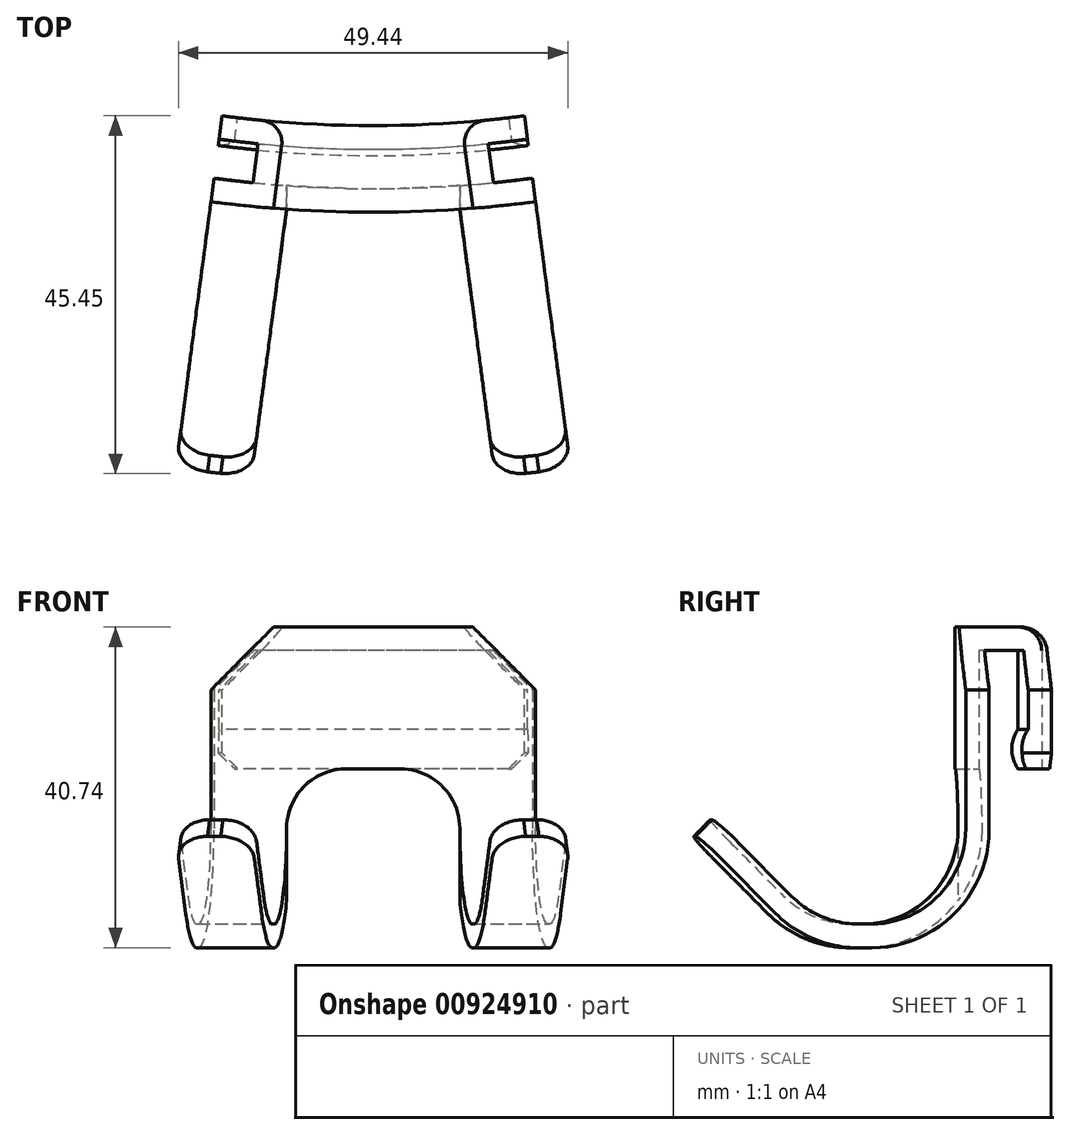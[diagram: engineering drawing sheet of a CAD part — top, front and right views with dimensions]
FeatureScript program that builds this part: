
annotation { "Feature Type Name" : "Feature", "Feature Type Description" : "" }
export const myFeature = defineFeature(function(context is Context, id is Id, definition is map)
    precondition{}
    {
        {
            var Q0;
            Q0=qCreatedBy(makeId("Right.planeOp"),FACE);
            var sketch = newSketch(context, id + "F0", { "sketchPlane" : qUnion([Q0])});
            skLineSegment(sketch, "E0", {"start": v(0, 0) * mm, "end": v(3, 0) * mm});
            skLineSegment(sketch, "E1", {"start": v(3, 0) * mm, "end": v(3, 13) * mm});
            skLineSegment(sketch, "E2", {"start": v(3, 13) * mm, "end": v(-8, 13) * mm});
            skLineSegment(sketch, "E3", {"start": v(-8, 13) * mm, "end": v(-8, -27.74) * mm});
            skLineSegment(sketch, "E4", {"start": v(0, 0) * mm, "end": v(0, 10) * mm});
            skLineSegment(sketch, "E5", {"start": v(0, 10) * mm, "end": v(-5, 10) * mm});
            skLineSegment(sketch, "E6", {"start": v(-5, 10) * mm, "end": v(-5, -27.74) * mm});
            skLineSegment(sketch, "E7", {"start": v(-5, -27.74) * mm, "end": v(-8, -27.74) * mm});
            skLineSegment(sketch, "E8", {"start": v(-8, -27.74) * mm, "end": v(-28, -27.74) * mm});
            skLineSegment(sketch, "E9", {"start": v(-28, -27.74) * mm, "end": v(-42.14, -13.6) * mm});
            skLineSegment(sketch, "E10", {"start": v(-42.14, -13.6) * mm, "end": v(-40.02, -11.48) * mm});
            skLineSegment(sketch, "E11", {"start": v(-40.02, -11.48) * mm, "end": v(-26.76, -24.74) * mm});
            skLineSegment(sketch, "E12", {"start": v(-26.76, -24.74) * mm, "end": v(-8, -24.74) * mm});
            skLineSegment(sketch, "E13", {"start": v(-5, 10) * mm, "end": v(-5, 13) * mm});
            skLineSegment(sketch, "E14", {"start": v(150, 0) * mm, "end": v(150, 35.9) * mm, "construction": true});
            skLineSegment(sketch, "E15", {"start": v(3, 0) * mm, "end": v(3, -5) * mm});
            skLineSegment(sketch, "E16", {"start": v(3, -5) * mm, "end": v(0, -5) * mm});
            skLineSegment(sketch, "E17", {"start": v(0, -5) * mm, "end": v(0, 0) * mm});
            skArc(sketch, "E18", {"start": v(0, 0) * mm, "mid": v(-0.8, -2.5) * mm, "end": v(0, -5) * mm});
            skSolve(sketch);
        }
        {
            var Q0;
            Q0=makeQuery(id+"F0.imprint","IMPRINT",FACE,{"disambiguationData":[TD([[makeQuery(id+"F0.imprint","IMPRINT",EDGE,{"derivedFrom":sQuery(id+"F0.wireOp",EDGE,"E0")}),1.0]])]});
            var Q1;
            Q1=makeQuery(id+"F0.imprint","IMPRINT",FACE,{"disambiguationData":[TD([[makeQuery(id+"F0.imprint","IMPRINT",EDGE,{"derivedFrom":sQuery(id+"F0.wireOp",EDGE,"E17")}),1.0]])]});
            var Q2;
            Q2=makeQuery(id+"F0.imprint","IMPRINT",FACE,{"disambiguationData":[TD([[makeQuery(id+"F0.imprint","IMPRINT",EDGE,{"derivedFrom":sQuery(id+"F0.wireOp",EDGE,"E0")}),-1.0]])]});
            var Q3;
            Q3=sQuery(id+"F0.wireOp",EDGE,"E14");
            revolve(context, id + "F1", {"surfaceOperationType" : NewSurfaceOperationType.NEW, "entities" : qUnion([Q0, Q1, Q2]), "axis" : qUnion([Q3]), "revolveType" : RevolveType.SYMMETRIC, "angle" : 15 * degree});
        }
        {
            var Q0;
            Q0=makeQuery(id+"F0.imprint","IMPRINT",FACE,{"disambiguationData":[TD([[makeQuery(id+"F0.imprint","IMPRINT",EDGE,{"derivedFrom":sQuery(id+"F0.wireOp",EDGE,"E6")}),-1.0]])]});
            var Q1;
            {var subQ0=sQuery(id+"F0.wireOp",EDGE,"E8");Q1=makeQuery(id+"F0.imprint","IMPRINT",FACE,{"disambiguationData":[TD([[makeQuery(id+"F0.imprint","IMPRINT",EDGE,{"derivedFrom":subQ0}),-1.0]])]});}
            var Q2;
            Q2=sQuery(id+"F0.wireOp",EDGE,"E14");
            revolve(context, id + "F2", {"operationType" : NewBodyOperationType.ADD, "surfaceOperationType" : NewSurfaceOperationType.NEW, "entities" : qUnion([Q0, Q1]), "axis" : qUnion([Q2]), "revolveType" : RevolveType.SYMMETRIC, "angle" : 15 * degree});
        }
        {
            var Q0;
            Q0=makeQuery(id+"F2.opRevolve","SWEPT_FACE",FACE,{"disambiguationData":[OSD([sQuery(id+"F0.wireOp",EDGE,"E12")])]});
            var sketch = newSketch(context, id + "F3", { "sketchPlane" : qUnion([Q0])});
            skLineSegment(sketch, "E19", {"start": v(-11, -7.62) * mm, "end": v(-15.57, -42.32) * mm});
            skLineSegment(sketch, "E20", {"start": v(-15.57, -42.32) * mm, "end": v(15.57, -42.32) * mm});
            skLineSegment(sketch, "E21", {"start": v(15.57, -42.32) * mm, "end": v(11, -7.62) * mm});
            skPoint(sketch, "E22", {"position": v(0, -42.32) * mm});
            skSolve(sketch);
        }
        {
            var Q0;
            Q0 = qSketchRegion(id + "F3", true);
            var Q1;
            {var subQ0=sQuery(id+"F3.wireOp",EDGE,"E19");var subQ1=sQuery(id+"F0.wireOp",EDGE,"E12");var subQ2=makeQuery(id+"F2.opRevolve","SWEPT_EDGE",EDGE,{"disambiguationData":[OSD([sQuery(id+"F0.wireOp",EDGE,"E3"),subQ1])]});var subQ3=makeQuery(id+"F3.imprint","INTERSECT",VERTEX,{"derivedFrom":[subQ2,subQ0]});Q1=makeQuery(id+"F3.imprint","IMPRINT",FACE,{"disambiguationData":[TD([[makeQuery(id+"F3.imprint","IMPRINT",EDGE,{"disambiguationData":[TD([[subQ3,-1.0]])],"derivedFrom":subQ0}),1.0]])]});}
            var Q2;
            {var subQ0=sQuery(id+"F3.wireOp",EDGE,"E20");Q2=makeQuery(id+"F3.imprint","IMPRINT",FACE,{"disambiguationData":[TD([[makeQuery(id+"F3.imprint","IMPRINT",EDGE,{"derivedFrom":subQ0}),1.0]])]});}
            extrude(context, id + "F4", {"entities" : qUnion([Q0, Q1, Q2]), "operationType" : NewBodyOperationType.REMOVE, "depth" : 81.8 * mm, "offsetDistance" : 25 * mm, "symmetric" : true});
        }
        {
            var Q0;
            {var subQ0=sQuery(id+"F0.wireOp",EDGE,"E12");var subQ1=sQuery(id+"F0.wireOp",EDGE,"E3");Q0=makeQuery(id+"F4.boolean.opBoolean","SPLIT",EDGE,{"disambiguationData":[TD([makeQuery(id+"F4.opExtrude","SWEPT_FACE",FACE,{"disambiguationData":[OSD([sQuery(id+"F3.wireOp",EDGE,"E19")])]})])],"derivedFrom":makeQuery(id+"F2.opRevolve","SWEPT_EDGE",EDGE,{"disambiguationData":[OSD([subQ1,subQ0])]})});}
            var Q1;
            {var subQ0=sQuery(id+"F0.wireOp",EDGE,"E12");var subQ1=sQuery(id+"F0.wireOp",EDGE,"E3");Q1=makeQuery(id+"F4.boolean.opBoolean","SPLIT",EDGE,{"disambiguationData":[TD([makeQuery(id+"F4.opExtrude","SWEPT_FACE",FACE,{"disambiguationData":[OSD([sQuery(id+"F3.wireOp",EDGE,"E21")])]})])],"derivedFrom":makeQuery(id+"F2.opRevolve","SWEPT_EDGE",EDGE,{"disambiguationData":[OSD([subQ1,subQ0])]})});}
            var Q2;
            {var subQ0=sQuery(id+"F0.wireOp",EDGE,"E12");var subQ1=sQuery(id+"F0.wireOp",EDGE,"E11");Q2=makeQuery(id+"F4.boolean.opBoolean","SPLIT",EDGE,{"disambiguationData":[TD([makeQuery(id+"F4.opExtrude","SWEPT_FACE",FACE,{"disambiguationData":[OSD([sQuery(id+"F3.wireOp",EDGE,"E19")])]})])],"derivedFrom":makeQuery(id+"F2.opRevolve","SWEPT_EDGE",EDGE,{"disambiguationData":[OSD([subQ1,subQ0])]})});}
            var Q3;
            {var subQ0=sQuery(id+"F0.wireOp",EDGE,"E12");var subQ1=sQuery(id+"F0.wireOp",EDGE,"E11");Q3=makeQuery(id+"F4.boolean.opBoolean","SPLIT",EDGE,{"disambiguationData":[TD([makeQuery(id+"F4.opExtrude","SWEPT_FACE",FACE,{"disambiguationData":[OSD([sQuery(id+"F3.wireOp",EDGE,"E21")])]})])],"derivedFrom":makeQuery(id+"F2.opRevolve","SWEPT_EDGE",EDGE,{"disambiguationData":[OSD([subQ1,subQ0])]})});}
            fillet(context, id + "F5", {"entities" : qUnion([Q0, Q1, Q2, Q3]), "radius" : 12.14 * mm, "tangentPropagation" : true, "allowEdgeOverflow" : false});
        }
        {
            var Q0;
            Q0=makeQuery(id+"F2.opRevolve","SWEPT_EDGE",EDGE,{"disambiguationData":[OSD([sQuery(id+"F0.wireOp",EDGE,"E6"),sQuery(id+"F0.wireOp",EDGE,"E7")])]});
            var Q1;
            {var subQ0=sQuery(id+"F0.wireOp",EDGE,"E9");var subQ1=sQuery(id+"F0.wireOp",EDGE,"E8");Q1=makeQuery(id+"F4.boolean.opBoolean","SPLIT",EDGE,{"disambiguationData":[TD([makeQuery(id+"F4.opExtrude","SWEPT_FACE",FACE,{"disambiguationData":[OSD([sQuery(id+"F3.wireOp",EDGE,"E21")])]})])],"derivedFrom":makeQuery(id+"F2.opRevolve","SWEPT_EDGE",EDGE,{"disambiguationData":[OSD([subQ1,subQ0])]})});}
            var Q2;
            {var subQ0=sQuery(id+"F0.wireOp",EDGE,"E9");var subQ1=sQuery(id+"F0.wireOp",EDGE,"E8");Q2=makeQuery(id+"F4.boolean.opBoolean","SPLIT",EDGE,{"disambiguationData":[TD([makeQuery(id+"F4.opExtrude","SWEPT_FACE",FACE,{"disambiguationData":[OSD([sQuery(id+"F3.wireOp",EDGE,"E19")])]})])],"derivedFrom":makeQuery(id+"F2.opRevolve","SWEPT_EDGE",EDGE,{"disambiguationData":[OSD([subQ1,subQ0])]})});}
            fillet(context, id + "F6", {"entities" : qUnion([Q0, Q1, Q2]), "radius" : 15 * mm, "tangentPropagation" : true, "allowEdgeOverflow" : false});
        }
        {
            var Q0;
            Q0=makeQuery(id+"F2.opRevolve","CAP_EDGE",EDGE,{"disambiguationData":[OSD([sQuery(id+"F0.wireOp",EDGE,"E10")])],"isStart":true});
            var Q1;
            Q1=makeQuery(id+"F4.boolean.opBoolean","INTERSECT",EDGE,{"derivedFrom":[makeQuery(id+"F2.opRevolve","SWEPT_FACE",FACE,{"disambiguationData":[OSD([sQuery(id+"F0.wireOp",EDGE,"E10")])]}),makeQuery(id+"F4.opExtrude","SWEPT_FACE",FACE,{"disambiguationData":[OSD([sQuery(id+"F3.wireOp",EDGE,"E19")])]})]});
            var Q2;
            Q2=makeQuery(id+"F4.boolean.opBoolean","INTERSECT",EDGE,{"derivedFrom":[makeQuery(id+"F2.opRevolve","SWEPT_FACE",FACE,{"disambiguationData":[OSD([sQuery(id+"F0.wireOp",EDGE,"E10")])]}),makeQuery(id+"F4.opExtrude","SWEPT_FACE",FACE,{"disambiguationData":[OSD([sQuery(id+"F3.wireOp",EDGE,"E21")])]})]});
            var Q3;
            Q3=makeQuery(id+"F2.opRevolve","CAP_EDGE",EDGE,{"disambiguationData":[OSD([sQuery(id+"F0.wireOp",EDGE,"E10")])],"isStart":false});
            fillet(context, id + "F7", {"entities" : qUnion([Q0, Q1, Q2, Q3]), "radius" : 4 * mm, "tangentPropagation" : true, "allowEdgeOverflow" : false});
        }
        {
            var Q0;
            Q0=qCreatedBy(makeId("Front.planeOp"),FACE);
            var sketch = newSketch(context, id + "F8", { "sketchPlane" : qUnion([Q0])});
            skPoint(sketch, "E23.0", {"position": v(-11, -12.6) * mm});
            skPoint(sketch, "E24.0", {"position": v(11, -12.6) * mm});
            skPoint(sketch, "E25.0", {"position": v(11, -21.74) * mm});
            skPoint(sketch, "E26.0", {"position": v(-11, -21.74) * mm});
            skLineSegment(sketch, "E27.bottom", {"start": v(-11, -5) * mm, "end": v(11, -5) * mm});
            skLineSegment(sketch, "E27.top", {"start": v(-11, -21.74) * mm, "end": v(11, -21.74) * mm});
            skLineSegment(sketch, "E27.left", {"start": v(-11, -5) * mm, "end": v(-11, -21.74) * mm});
            skLineSegment(sketch, "E27.right", {"start": v(11, -5) * mm, "end": v(11, -21.74) * mm});
            skLineSegment(sketch, "E28.0", {"start": v(19.19, -5) * mm, "end": v(-19.19, -5) * mm});
            skSolve(sketch);
        }
        {
            var Q0;
            Q0 = qSketchRegion(id + "F8", true);
            extrude(context, id + "F9", {"entities" : qUnion([Q0]), "operationType" : NewBodyOperationType.REMOVE, "endBound" : BoundingType.THROUGH_ALL, "depth" : 25 * mm, "offsetDistance" : 25 * mm});
        }
        {
            var Q0;
            Q0=makeQuery(id+"F9.boolean.opBoolean","COPY",EDGE,{"derivedFrom":makeQuery(id+"F9.opExtrude","SWEPT_EDGE",EDGE,{"disambiguationData":[OSD([sQuery(id+"F8.wireOp",EDGE,"E27.bottom"),sQuery(id+"F8.wireOp",EDGE,"E27.left")])]})});
            var Q1;
            Q1=makeQuery(id+"F9.boolean.opBoolean","COPY",EDGE,{"derivedFrom":makeQuery(id+"F9.opExtrude","SWEPT_EDGE",EDGE,{"disambiguationData":[OSD([sQuery(id+"F8.wireOp",EDGE,"E27.bottom"),sQuery(id+"F8.wireOp",EDGE,"E27.right")])]})});
            fillet(context, id + "F10", {"entities" : qUnion([Q0, Q1]), "radius" : 7.6 * mm, "tangentPropagation" : true, "allowEdgeOverflow" : false});
        }
        {
            var Q0;
            Q0=makeQuery(id+"F1.opRevolve","SWEPT_EDGE",EDGE,{"disambiguationData":[OSD([sQuery(id+"F0.wireOp",EDGE,"E1"),sQuery(id+"F0.wireOp",EDGE,"E2")])]});
            var Q1;
            Q1=makeQuery(id+"F2.opRevolve","SWEPT_EDGE",EDGE,{"disambiguationData":[OSD([sQuery(id+"F0.wireOp",EDGE,"E2"),sQuery(id+"F0.wireOp",EDGE,"E3")])]});
            fillet(context, id + "F11", {"entities" : qUnion([Q0, Q1]), "radius" : 3 * mm, "tangentPropagation" : true, "allowEdgeOverflow" : false});
        }
        {
            var Q0;
            {var subQ0=sQuery(id+"F0.wireOp",EDGE,"E2");Q0=makeQuery(id+"F2.boolean.opBoolean","MERGE",EDGE,{"derivedFrom":[makeQuery(id+"F1.opRevolve","CAP_EDGE",EDGE,{"disambiguationData":[OSD([subQ0])],"isStart":false}),makeQuery(id+"F2.opRevolve","CAP_EDGE",EDGE,{"disambiguationData":[OSD([subQ0])],"isStart":false})]});}
            var Q1;
            {var subQ0=sQuery(id+"F0.wireOp",EDGE,"E2");Q1=makeQuery(id+"F2.boolean.opBoolean","MERGE",EDGE,{"derivedFrom":[makeQuery(id+"F1.opRevolve","CAP_EDGE",EDGE,{"disambiguationData":[OSD([subQ0])],"isStart":true}),makeQuery(id+"F2.opRevolve","CAP_EDGE",EDGE,{"disambiguationData":[OSD([subQ0])],"isStart":true})]});}
            chamfer(context, id + "F12", {"entities" : qUnion([Q0, Q1]), "width" : 8 * mm});
        }
        {
            var Q0;
            Q0=makeQuery(id+"F1.opRevolve","CAP_EDGE",EDGE,{"disambiguationData":[OSD([sQuery(id+"F0.wireOp",EDGE,"E16")])],"isStart":false});
            var Q1;
            Q1=makeQuery(id+"F1.opRevolve","CAP_EDGE",EDGE,{"disambiguationData":[OSD([sQuery(id+"F0.wireOp",EDGE,"E16")])],"isStart":true});
            chamfer(context, id + "F13", {"entities" : qUnion([Q0, Q1]), "width" : 2 * mm, "tangentPropagation" : true});
        }
    });
